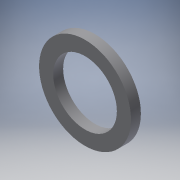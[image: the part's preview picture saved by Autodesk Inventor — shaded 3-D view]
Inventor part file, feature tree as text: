
AUTODESK INVENTOR PART (.ipt)
format: ipt  version: 2018 (Build 220112000, 112)  size: 101,376 bytes
history: native  units: in
note: dims shown in document units (in); Inventor stores cm internally (conversion verified against a paired STEP export)
features: extrude x1, sketch x1
ambient origin geometry x8: Origin, YZ Plane, XZ Plane, XY Plane, X Axis, Y Axis, Z Axis, Center Point
bodies: Solid1 (feature_tree)
feature tree (2):
  extrude  "Extrusion1"  Depth=0.0276in
  sketch  "Sketch1"  dims[d0=0.2559in d1=0.1772in d2=0.0276in d3=0.0in]
